# Revit family: ALL3_63_UN_Downlighter_ETK
name_source: partatom
category: Lighting Fixtures
revit_build: Autodesk Revit 2017 (Build: 20190508_0315(x64)
units: mm (PartAtom-declared; Revit-internal decimal feet)

## family parameters
Always vertical = Yes
Cut with Voids When Loaded = No
Light Source = No
OmniClass Number = 23.80.70.11.14.11
OmniClass Title = Downlights
Part Type = Normal
Room Calculation Point = Yes
Round Connector Dimension = Use Diameter
Shared = No
Work Plane-Based = No

## types (16) — shared parameters
Assembly Code = 63.0
Bundle = 65°
Description = Downlighter
IfcExportAs = IfcLightFixtureType
IfcExportType = USERDEFINED
Lamp = LED
Luminaire_Body_Material = Aluminum 7175 T73 0 Hot Formed
Luminaire_Ring_Material = PPS Plastic
Manufacturer = ETK B.V.
Model = ALL.3
URL = https://www.etk.nl
Voltage = 230 V

## per-type parameters (varying)
| type | Apparent Load | Light Source | Wattage Comments |
| ALL.3100.15 - 28W / 3150lm / 3000K | 28 VA | ALL.3 - Lightsource : ALL.3100.15 - 28W / 3150lm / 3000K | 28W |
| ALL.3200.15 - 28W / 3300lm / 4000K | 28 VA | ALL.3 - Lightsource : ALL.3200.15 - 28W / 3300lm / 4000K | 28W |
| ALL.3300.15 - 32W / 3650lm / 3000K | 32 VA | ALL.3 - Lightsource : ALL.3300.15 - 32W / 3650lm / 3000K | 32W |
| ALL.3400.15 - 32W / 3800lm / 3000K | 32 VA | ALL.3 - Lightsource : ALL.3400.15 - 32W / 3650lm / 3000K | 32W |
| ALL.3103.15 - 28W / 3150lm / 3000K | 28 VA | ALL.3 - Lightsource : ALL.3103.15 - 28W / 3150lm / 3000K | 28W |
| ALL.3203.15 - 28W / 3300lm / 4000K | 28 VA | ALL.3 - Lightsource : ALL.3203.15 - 28W / 3300lm / 4000K | 28W |
| ALL.3303.15 - 32W / 3650lm / 3000K | 32 VA | ALL.3 - Lightsource : ALL.3303.15 - 32W / 3650lm / 3000K | 32W |
| ALL.3403.15 - 32W / 3800lm / 3000K | 32 VA | ALL.3 - Lightsource : ALL.3403.15 - 32W / 3650lm / 3000K | 32W |
| ALL.3110.15 - 28W / 3150lm / 3000K | 28 VA | ALL.3 - Lightsource : ALL.3110.15 - 28W / 3150lm / 3000K | 28W |
| ALL.3210.15 - 28W / 3300lm / 4000K | 28 VA | ALL.3 - Lightsource : ALL.3210.15 - 28W / 3300lm / 4000K | 28W |
| ALL.3310.15 - 32W / 3650lm / 3000K | 32 VA | ALL.3 - Lightsource : ALL.3310.15 - 32W / 3650lm / 3000K | 32W |
| ALL.3410.15 - 32W / 3800lm / 3000K | 32 VA | ALL.3 - Lightsource : ALL.3410.15 - 32W / 3650lm / 3000K | 32W |
| ALL.3113.15 - 28W / 3150lm / 3000K | 28 VA | ALL.3 - Lightsource : ALL.3113.15 - 28W / 3150lm / 3000K | 28W |
| ALL.3213.15 - 28W / 3300lm / 4000K | 28 VA | ALL.3 - Lightsource : ALL.3213.15 - 28W / 3300lm / 4000K | 28W |
| ALL.3313.15 - 32W / 3650lm / 3000K | 32 VA | ALL.3 - Lightsource : ALL.3313.15 - 32W / 3650lm / 3000K | 32W |
| ALL.3413.15 - 32W / 3800lm / 3000K | 32 VA | ALL.3 - Lightsource : ALL.3413.15 - 32W / 3650lm / 3000K | 32W |

## geometry (parser evidence)
native form markers: Sweep x5
no freeform markers — native parametric forms only
